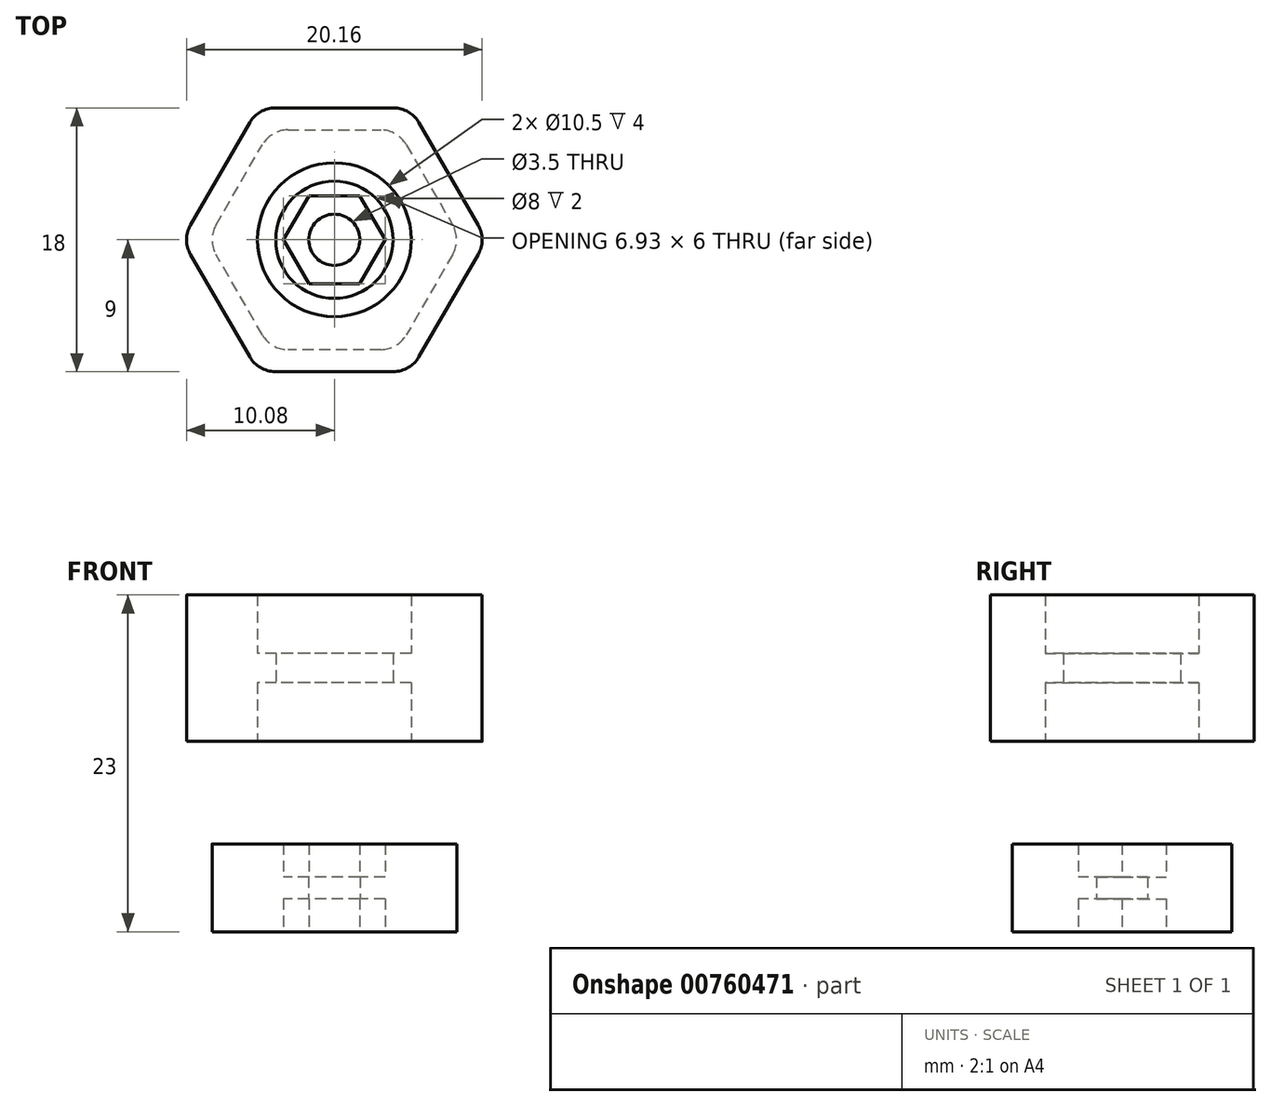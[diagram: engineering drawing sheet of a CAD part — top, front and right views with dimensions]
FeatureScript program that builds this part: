
annotation { "Feature Type Name" : "Feature", "Feature Type Description" : "" }
export const myFeature = defineFeature(function(context is Context, id is Id, definition is map)
    precondition{}
    {
        {
            var Q0;
            Q0=qCreatedBy(makeId("Top.planeOp"),FACE);
            var sketch = newSketch(context, id + "F0", { "sketchPlane" : qUnion([Q0])});
            skCircle(sketch, "E0", {"center": v(0, 0) * mm, "radius": 4 * mm});
            skCircle(sketch, "E1", {"center": v(0, 0) * mm, "radius": 5.25 * mm});
            skCircle(sketch, "E2.cCircle", {"center": v(0, 0) * mm, "radius": 9 * mm, "construction": true});
            skLineSegment(sketch, "E2.0", {"start": v(-5.2, 9) * mm, "end": v(5.2, 9) * mm});
            skLineSegment(sketch, "E2.1", {"start": v(5.2, 9) * mm, "end": v(10.4, 0) * mm});
            skLineSegment(sketch, "E2.2", {"start": v(10.4, 0) * mm, "end": v(5.2, -9) * mm});
            skLineSegment(sketch, "E2.3", {"start": v(5.2, -9) * mm, "end": v(-5.2, -9) * mm});
            skLineSegment(sketch, "E2.4", {"start": v(-5.2, -9) * mm, "end": v(-10.4, 0) * mm});
            skLineSegment(sketch, "E2.5", {"start": v(-10.4, 0) * mm, "end": v(-5.2, 9) * mm});
            skPoint(sketch, "E2.0.midPoint", {"position": v(0, 9) * mm});
            skSolve(sketch);
        }
        {
            var Q0;
            Q0 = qSketchRegion(id + "F0", true);
            extrude(context, id + "F1", {"entities" : qUnion([Q0]), "endBound" : BoundingType.SYMMETRIC, "depth" : 10 * mm, "offsetDistance" : 25 * mm});
        }
        {
            var Q0;
            Q0=makeQuery(id+"F0.imprint","IMPRINT",FACE,{"disambiguationData":[TD([[makeQuery(id+"F0.imprint","IMPRINT",EDGE,{"derivedFrom":sQuery(id+"F0.wireOp",EDGE,"E0")}),-1.0]])]});
            extrude(context, id + "F2", {"entities" : qUnion([Q0]), "operationType" : NewBodyOperationType.ADD, "endBound" : BoundingType.SYMMETRIC, "depth" : 2 * mm, "offsetDistance" : 25 * mm});
        }
        {
            var Q0;
            Q0=makeQuery(id+"F1.opExtrude","SWEPT_BODY",BODY,{"disambiguationData":[OSD([sQuery(id+"F0.wireOp",EDGE,"E1"),sQuery(id+"F0.wireOp",EDGE,"E2.0"),sQuery(id+"F0.wireOp",EDGE,"E2.1"),sQuery(id+"F0.wireOp",EDGE,"E2.2"),sQuery(id+"F0.wireOp",EDGE,"E2.3"),sQuery(id+"F0.wireOp",EDGE,"E2.4"),sQuery(id+"F0.wireOp",EDGE,"E2.5")])]});
            transform(context, id + "F3", {"entities" : qUnion([Q0]), "transformType" : TransformType.TRANSLATION_3D, "dx" : 0 * mm, "dy" : 0 * mm, "dz" : 15 * mm, "makeCopy" : false});
        }
        {
            var Q0;
            Q0=qCreatedBy(makeId("Top.planeOp"),FACE);
            var sketch = newSketch(context, id + "F4", { "sketchPlane" : qUnion([Q0])});
            skCircle(sketch, "E3", {"center": v(0, 0) * mm, "radius": 1.75 * mm});
            skCircle(sketch, "E4.cCircle", {"center": v(0, 0) * mm, "radius": 3 * mm, "construction": true});
            skLineSegment(sketch, "E4.0", {"start": v(1.73, -3) * mm, "end": v(-1.73, -3) * mm});
            skLineSegment(sketch, "E4.1", {"start": v(-1.73, -3) * mm, "end": v(-3.46, 0) * mm});
            skLineSegment(sketch, "E4.2", {"start": v(-3.46, 0) * mm, "end": v(-1.73, 3) * mm});
            skLineSegment(sketch, "E4.3", {"start": v(-1.73, 3) * mm, "end": v(1.73, 3) * mm});
            skLineSegment(sketch, "E4.4", {"start": v(1.73, 3) * mm, "end": v(3.46, 0) * mm});
            skLineSegment(sketch, "E4.5", {"start": v(3.46, 0) * mm, "end": v(1.73, -3) * mm});
            skPoint(sketch, "E4.0.midPoint", {"position": v(0, -3) * mm});
            skCircle(sketch, "E5.cCircle", {"center": v(0, 0) * mm, "radius": 7.5 * mm, "construction": true});
            skLineSegment(sketch, "E5.0", {"start": v(4.33, -7.5) * mm, "end": v(-4.33, -7.5) * mm});
            skLineSegment(sketch, "E5.1", {"start": v(-4.33, -7.5) * mm, "end": v(-8.66, 0) * mm});
            skLineSegment(sketch, "E5.2", {"start": v(-8.66, 0) * mm, "end": v(-4.33, 7.5) * mm});
            skLineSegment(sketch, "E5.3", {"start": v(-4.33, 7.5) * mm, "end": v(4.33, 7.5) * mm});
            skLineSegment(sketch, "E5.4", {"start": v(4.33, 7.5) * mm, "end": v(8.66, 0) * mm});
            skLineSegment(sketch, "E5.5", {"start": v(8.66, 0) * mm, "end": v(4.33, -7.5) * mm});
            skPoint(sketch, "E5.0.midPoint", {"position": v(0, -7.5) * mm});
            skSolve(sketch);
        }
        {
            var Q0;
            Q0=makeQuery(id+"F4.imprint","IMPRINT",FACE,{"disambiguationData":[TD([[makeQuery(id+"F4.imprint","IMPRINT",EDGE,{"derivedFrom":sQuery(id+"F4.wireOp",EDGE,"E4.0")}),1.0]])]});
            extrude(context, id + "F5", {"entities" : qUnion([Q0]), "endBound" : BoundingType.SYMMETRIC, "depth" : 6 * mm, "offsetDistance" : 25 * mm});
        }
        {
            var Q0;
            Q0=makeQuery(id+"F4.imprint","IMPRINT",FACE,{"disambiguationData":[TD([[makeQuery(id+"F4.imprint","IMPRINT",EDGE,{"derivedFrom":sQuery(id+"F4.wireOp",EDGE,"E3")}),-1.0]])]});
            extrude(context, id + "F6", {"entities" : qUnion([Q0]), "operationType" : NewBodyOperationType.ADD, "endBound" : BoundingType.SYMMETRIC, "depth" : 1.5 * mm, "offsetDistance" : 25 * mm, "hasSecondDirection" : true, "secondDirectionOppositeDirection" : true, "secondDirectionDepth" : 1 * mm});
        }
        {
            var Q0;
            Q0=makeQuery(id+"F1.opExtrude","SWEPT_EDGE",EDGE,{"disambiguationData":[OSD([sQuery(id+"F0.wireOp",EDGE,"E2.0"),sQuery(id+"F0.wireOp",EDGE,"E2.5")])]});
            var Q1;
            Q1=makeQuery(id+"F1.opExtrude","SWEPT_EDGE",EDGE,{"disambiguationData":[OSD([sQuery(id+"F0.wireOp",EDGE,"E2.0"),sQuery(id+"F0.wireOp",EDGE,"E2.1")])]});
            var Q2;
            Q2=makeQuery(id+"F1.opExtrude","SWEPT_EDGE",EDGE,{"disambiguationData":[OSD([sQuery(id+"F0.wireOp",EDGE,"E2.3"),sQuery(id+"F0.wireOp",EDGE,"E2.4")])]});
            var Q3;
            Q3=makeQuery(id+"F1.opExtrude","SWEPT_EDGE",EDGE,{"disambiguationData":[OSD([sQuery(id+"F0.wireOp",EDGE,"E2.2"),sQuery(id+"F0.wireOp",EDGE,"E2.3")])]});
            var Q4;
            Q4=makeQuery(id+"F1.opExtrude","SWEPT_EDGE",EDGE,{"disambiguationData":[OSD([sQuery(id+"F0.wireOp",EDGE,"E2.1"),sQuery(id+"F0.wireOp",EDGE,"E2.2")])]});
            var Q5;
            Q5=makeQuery(id+"F1.opExtrude","SWEPT_EDGE",EDGE,{"disambiguationData":[OSD([sQuery(id+"F0.wireOp",EDGE,"E2.4"),sQuery(id+"F0.wireOp",EDGE,"E2.5")])]});
            var Q6;
            Q6=makeQuery(id+"F5.opExtrude","SWEPT_EDGE",EDGE,{"disambiguationData":[OSD([sQuery(id+"F4.wireOp",EDGE,"E5.2"),sQuery(id+"F4.wireOp",EDGE,"E5.3")])]});
            var Q7;
            Q7=makeQuery(id+"F5.opExtrude","SWEPT_EDGE",EDGE,{"disambiguationData":[OSD([sQuery(id+"F4.wireOp",EDGE,"E5.3"),sQuery(id+"F4.wireOp",EDGE,"E5.4")])]});
            var Q8;
            Q8=makeQuery(id+"F5.opExtrude","SWEPT_EDGE",EDGE,{"disambiguationData":[OSD([sQuery(id+"F4.wireOp",EDGE,"E5.1"),sQuery(id+"F4.wireOp",EDGE,"E5.2")])]});
            var Q9;
            Q9=makeQuery(id+"F5.opExtrude","SWEPT_EDGE",EDGE,{"disambiguationData":[OSD([sQuery(id+"F4.wireOp",EDGE,"E5.0"),sQuery(id+"F4.wireOp",EDGE,"E5.1")])]});
            var Q10;
            Q10=makeQuery(id+"F5.opExtrude","SWEPT_EDGE",EDGE,{"disambiguationData":[OSD([sQuery(id+"F4.wireOp",EDGE,"E5.0"),sQuery(id+"F4.wireOp",EDGE,"E5.5")])]});
            var Q11;
            Q11=makeQuery(id+"F5.opExtrude","SWEPT_EDGE",EDGE,{"disambiguationData":[OSD([sQuery(id+"F4.wireOp",EDGE,"E5.4"),sQuery(id+"F4.wireOp",EDGE,"E5.5")])]});
            fillet(context, id + "F7", {"entities" : qUnion([Q0, Q1, Q2, Q3, Q4, Q5, Q6, Q7, Q8, Q9, Q10, Q11]), "radius" : 2 * mm, "tangentPropagation" : true, "allowEdgeOverflow" : false});
        }
    });
